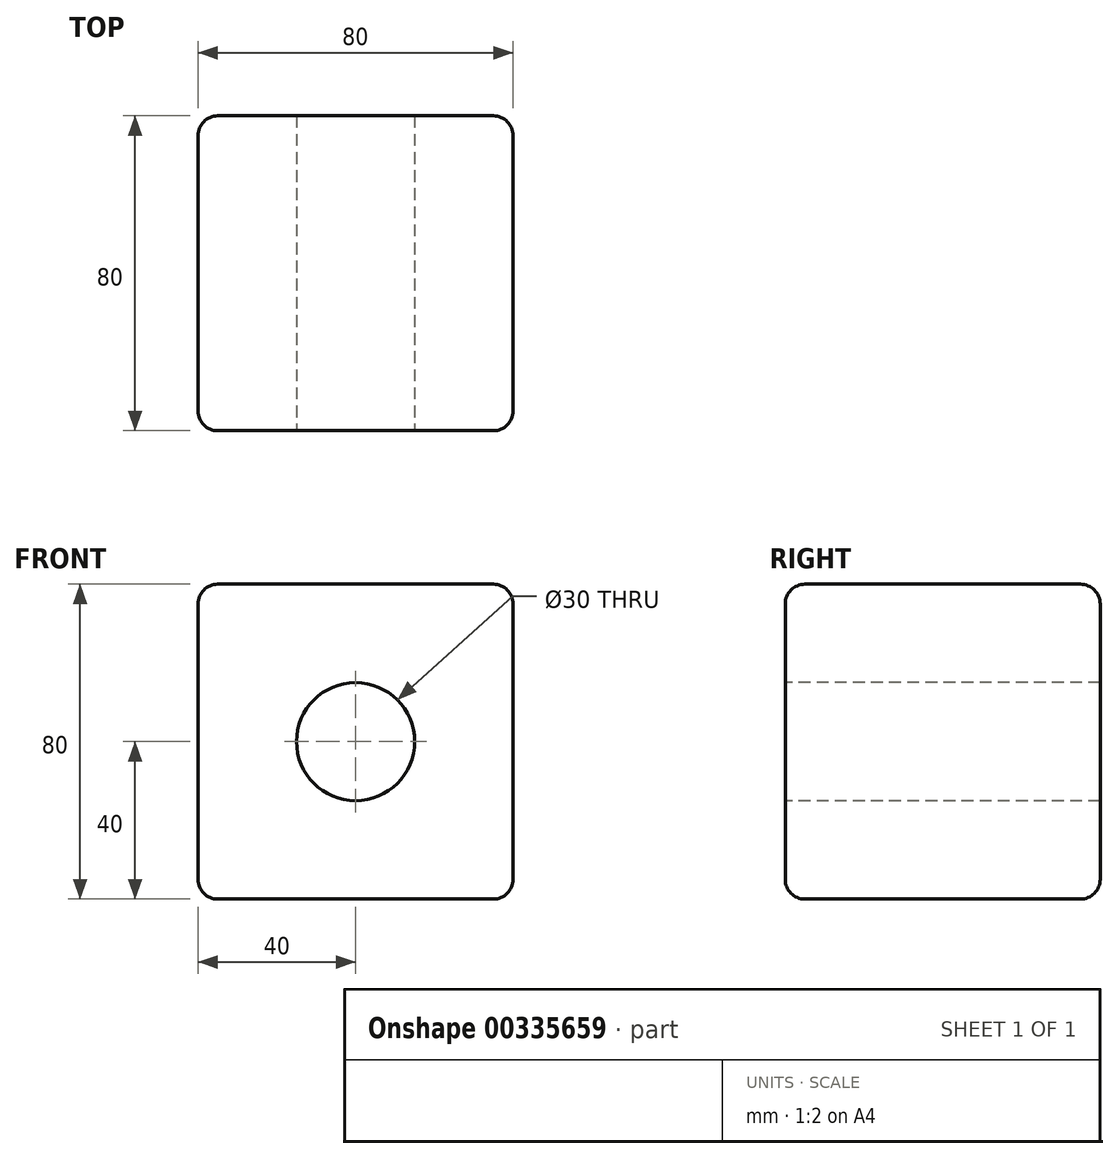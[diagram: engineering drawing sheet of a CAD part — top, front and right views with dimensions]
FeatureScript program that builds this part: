
annotation { "Feature Type Name" : "Feature", "Feature Type Description" : "" }
export const myFeature = defineFeature(function(context is Context, id is Id, definition is map)
    precondition{}
    {
        {
            var Q0;
            Q0=qCreatedBy(makeId("Top.planeOp"),FACE);
            var sketch = newSketch(context, id + "F0", { "sketchPlane" : qUnion([Q0])});
            skLineSegment(sketch, "E0.bottom", {"start": v(-40, 40) * mm, "end": v(40, 40) * mm});
            skLineSegment(sketch, "E0.top", {"start": v(-40, -40) * mm, "end": v(40, -40) * mm});
            skLineSegment(sketch, "E0.left", {"start": v(-40, 40) * mm, "end": v(-40, -40) * mm});
            skLineSegment(sketch, "E0.right", {"start": v(40, 40) * mm, "end": v(40, -40) * mm});
            skPoint(sketch, "E0.middle", {"position": v(0, 0) * mm});
            skSolve(sketch);
        }
        {
            var Q0;
            Q0=makeQuery(id+"F0.imprint","IMPRINT",FACE,{"disambiguationData":[TD([[makeQuery(id+"F0.imprint","IMPRINT",EDGE,{"derivedFrom":sQuery(id+"F0.wireOp",EDGE,"E0.bottom")}),-1.0]])]});
            extrude(context, id + "F1", {"entities" : qUnion([Q0]), "endBound" : BoundingType.SYMMETRIC, "depth" : 80 * mm});
        }
        {
            var Q0;
            Q0=makeQuery(id+"F1.opExtrude","CAP_EDGE",EDGE,{"disambiguationData":[OSD([sQuery(id+"F0.wireOp",EDGE,"E0.top")])],"isStart":false});
            var Q1;
            Q1=makeQuery(id+"F1.opExtrude","SWEPT_EDGE",EDGE,{"disambiguationData":[OSD([sQuery(id+"F0.wireOp",EDGE,"E0.top"),sQuery(id+"F0.wireOp",EDGE,"E0.left")])]});
            var Q2;
            Q2=makeQuery(id+"F1.opExtrude","SWEPT_EDGE",EDGE,{"disambiguationData":[OSD([sQuery(id+"F0.wireOp",EDGE,"E0.top"),sQuery(id+"F0.wireOp",EDGE,"E0.right")])]});
            var Q3;
            Q3=makeQuery(id+"F1.opExtrude","CAP_EDGE",EDGE,{"disambiguationData":[OSD([sQuery(id+"F0.wireOp",EDGE,"E0.top")])],"isStart":true});
            var Q4;
            Q4=makeQuery(id+"F1.opExtrude","CAP_EDGE",EDGE,{"disambiguationData":[OSD([sQuery(id+"F0.wireOp",EDGE,"E0.right")])],"isStart":false});
            var Q5;
            Q5=makeQuery(id+"F1.opExtrude","SWEPT_EDGE",EDGE,{"disambiguationData":[OSD([sQuery(id+"F0.wireOp",EDGE,"E0.bottom"),sQuery(id+"F0.wireOp",EDGE,"E0.right")])]});
            var Q6;
            Q6=makeQuery(id+"F1.opExtrude","CAP_EDGE",EDGE,{"disambiguationData":[OSD([sQuery(id+"F0.wireOp",EDGE,"E0.right")])],"isStart":true});
            var Q7;
            Q7=makeQuery(id+"F1.opExtrude","CAP_EDGE",EDGE,{"disambiguationData":[OSD([sQuery(id+"F0.wireOp",EDGE,"E0.bottom")])],"isStart":false});
            var Q8;
            Q8=makeQuery(id+"F1.opExtrude","SWEPT_EDGE",EDGE,{"disambiguationData":[OSD([sQuery(id+"F0.wireOp",EDGE,"E0.bottom"),sQuery(id+"F0.wireOp",EDGE,"E0.left")])]});
            var Q9;
            Q9=makeQuery(id+"F1.opExtrude","CAP_EDGE",EDGE,{"disambiguationData":[OSD([sQuery(id+"F0.wireOp",EDGE,"E0.bottom")])],"isStart":true});
            fillet(context, id + "F2", {"entities" : qUnion([Q0, Q1, Q2, Q3, Q4, Q5, Q6, Q7, Q8, Q9]), "radius" : 5 * mm, "tangentPropagation" : true, "allowEdgeOverflow" : false});
        }
        {
            var Q0;
            {var subQ0=sQuery(id+"F0.wireOp",EDGE,"E0.left");Q0=makeQuery(id+"F2.opFillet","BLEND_EDGE",EDGE,{"blendedFrom":[makeQuery(id+"F1.opExtrude","SWEPT_EDGE",EDGE,{"disambiguationData":[OSD([sQuery(id+"F0.wireOp",EDGE,"E0.bottom"),subQ0])]}),makeQuery(id+"F1.opExtrude","SWEPT_FACE",FACE,{"disambiguationData":[OSD([subQ0])]})],"blendedInto":[makeQuery(id+"F1.opExtrude","SWEPT_FACE",FACE,{"disambiguationData":[OSD([subQ0])]})]});}
            var Q1;
            Q1=makeQuery(id+"F2.opFillet","BLEND_FACE",FACE,{"disambiguationData":[OSD([sQuery(id+"F0.wireOp",EDGE,"E0.bottom"),sQuery(id+"F0.wireOp",EDGE,"E0.left")])]});
            fillet(context, id + "F3", {"entities" : qUnion([Q0, Q1]), "radius" : 5 * mm, "tangentPropagation" : true, "allowEdgeOverflow" : false});
        }
        {
            var Q0;
            Q0=makeQuery(id+"F1.opExtrude","SWEPT_FACE",FACE,{"disambiguationData":[OSD([sQuery(id+"F0.wireOp",EDGE,"E0.top")])]});
            var sketch = newSketch(context, id + "F4", { "sketchPlane" : qUnion([Q0])});
            skCircle(sketch, "E1", {"center": v(0, 0) * mm, "radius": 15 * mm});
            skSolve(sketch);
        }
        {
            var Q0;
            Q0=makeQuery(id+"F4.imprint","IMPRINT",FACE,{"disambiguationData":[TD([[makeQuery(id+"F4.imprint","IMPRINT",EDGE,{"derivedFrom":sQuery(id+"F4.wireOp",EDGE,"E1")}),1.0]])]});
            extrude(context, id + "F5", {"entities" : qUnion([Q0]), "operationType" : NewBodyOperationType.REMOVE, "endBound" : BoundingType.THROUGH_ALL, "oppositeDirection" : true, "depth" : 25 * mm});
        }
    });
